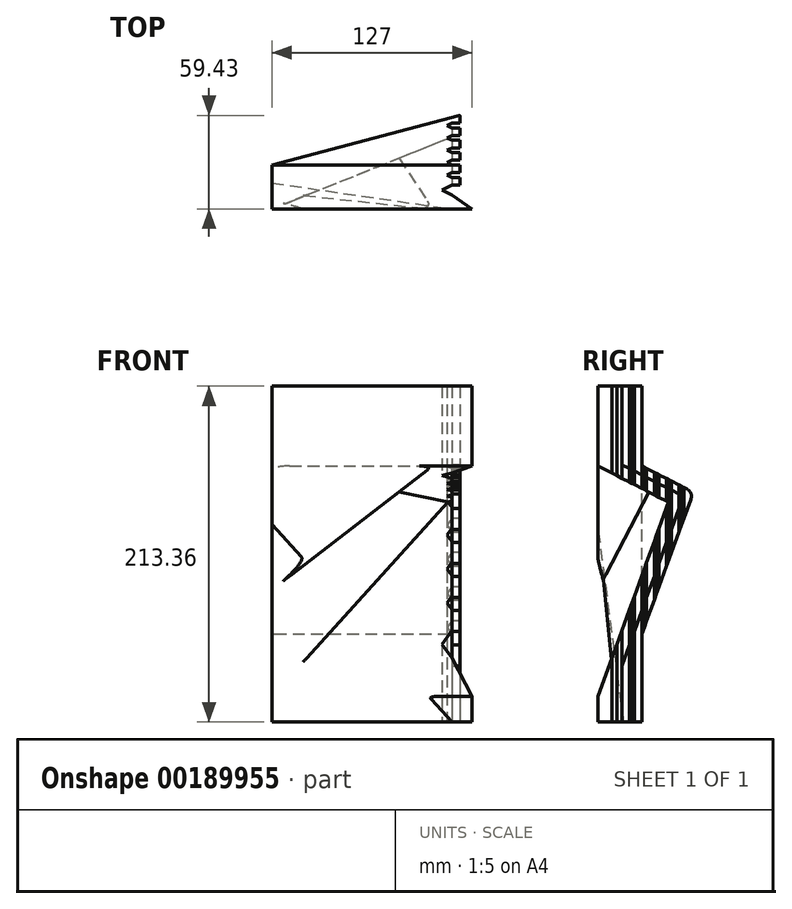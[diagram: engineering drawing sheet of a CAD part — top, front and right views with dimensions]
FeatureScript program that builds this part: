
annotation { "Feature Type Name" : "Feature", "Feature Type Description" : "" }
export const myFeature = defineFeature(function(context is Context, id is Id, definition is map)
    precondition{}
    {
        {
            var Q0;
            Q0=qCreatedBy(makeId("Top.planeOp"),FACE);
            var sketch = newSketch(context, id + "F0", { "sketchPlane" : qUnion([Q0])});
            skLineSegment(sketch, "E0", {"start": v(0, 6.35) * mm, "end": v(5.08, 6.35) * mm});
            skLineSegment(sketch, "E1", {"start": v(5.08, 6.35) * mm, "end": v(5.08, 11.18) * mm});
            skLineSegment(sketch, "E2", {"start": v(5.08, 11.18) * mm, "end": v(0, 11.18) * mm});
            skLineSegment(sketch, "E3", {"start": v(0, 11.18) * mm, "end": v(0, 14.22) * mm});
            skLineSegment(sketch, "E4", {"start": v(0, 14.22) * mm, "end": v(5.08, 14.22) * mm});
            skLineSegment(sketch, "E5", {"start": v(5.08, 14.22) * mm, "end": v(5.08, 19.05) * mm});
            skLineSegment(sketch, "E6", {"start": v(5.08, 19.05) * mm, "end": v(0, 19.05) * mm});
            skLineSegment(sketch, "E7", {"start": v(0, 19.05) * mm, "end": v(0, 22.1) * mm});
            skLineSegment(sketch, "E8", {"start": v(0, 22.1) * mm, "end": v(5.08, 22.1) * mm});
            skLineSegment(sketch, "E9", {"start": v(5.08, 22.1) * mm, "end": v(5.08, 26.92) * mm});
            skLineSegment(sketch, "E10", {"start": v(5.08, 26.92) * mm, "end": v(0, 26.92) * mm});
            skLineSegment(sketch, "E11", {"start": v(0, 26.92) * mm, "end": v(0, 29.97) * mm});
            skLineSegment(sketch, "E12", {"start": v(0, 29.97) * mm, "end": v(5.08, 29.97) * mm});
            skLineSegment(sketch, "E13", {"start": v(5.08, 29.97) * mm, "end": v(5.08, 34.8) * mm});
            skLineSegment(sketch, "E14", {"start": v(5.08, 34.8) * mm, "end": v(0, 34.8) * mm});
            skLineSegment(sketch, "E15", {"start": v(0, 34.8) * mm, "end": v(0, 37.85) * mm});
            skLineSegment(sketch, "E16", {"start": v(0, 37.85) * mm, "end": v(5.08, 37.85) * mm});
            skLineSegment(sketch, "E17", {"start": v(5.08, 37.85) * mm, "end": v(5.08, 42.67) * mm});
            skLineSegment(sketch, "E18", {"start": v(5.08, 42.67) * mm, "end": v(0, 42.67) * mm});
            skLineSegment(sketch, "E19", {"start": v(-114.3, 0) * mm, "end": v(0, 0) * mm});
            skLineSegment(sketch, "E20", {"start": v(0, 0) * mm, "end": v(0, 6.35) * mm});
            skLineSegment(sketch, "E21", {"start": v(0, 42.67) * mm, "end": v(0, 45.72) * mm});
            skLineSegment(sketch, "E22", {"start": v(-114.3, 53.6) * mm, "end": v(-114.3, 0) * mm});
            skLineSegment(sketch, "E23", {"start": v(0, 45.72) * mm, "end": v(5.08, 45.72) * mm});
            skLineSegment(sketch, "E24", {"start": v(5.08, 45.72) * mm, "end": v(5.08, 50.55) * mm});
            skLineSegment(sketch, "E25", {"start": v(5.08, 50.55) * mm, "end": v(0, 50.55) * mm});
            skLineSegment(sketch, "E26", {"start": v(0, 50.55) * mm, "end": v(0, 53.6) * mm});
            skLineSegment(sketch, "E27", {"start": v(0, 53.6) * mm, "end": v(-114.3, 53.6) * mm});
            skLineSegment(sketch, "E28", {"start": v(0, 0) * mm, "end": v(0, -8.89) * mm});
            skLineSegment(sketch, "E29", {"start": v(0, -8.89) * mm, "end": v(-114.3, -8.9) * mm});
            skLineSegment(sketch, "E30", {"start": v(-114.3, -8.9) * mm, "end": v(-114.3, 0) * mm});
            skLineSegment(sketch, "E31", {"start": v(0, -8.89) * mm, "end": v(12.7, -8.89) * mm});
            skLineSegment(sketch, "E32", {"start": v(12.7, -8.89) * mm, "end": v(0, 0) * mm});
            skLineSegment(sketch, "E33", {"start": v(0, 0) * mm, "end": v(-6.35, 3.17) * mm});
            skLineSegment(sketch, "E34", {"start": v(-6.35, 3.18) * mm, "end": v(0, 6.35) * mm});
            skLineSegment(sketch, "E35", {"start": v(0, 11.18) * mm, "end": v(-3.05, 12.7) * mm});
            skLineSegment(sketch, "E36", {"start": v(-3.05, 12.7) * mm, "end": v(0, 14.22) * mm});
            skLineSegment(sketch, "E37", {"start": v(0, 19.05) * mm, "end": v(-3.05, 20.57) * mm});
            skPoint(sketch, "E37.endSnap0", {"position": v(0, 20.57) * mm});
            skLineSegment(sketch, "E38", {"start": v(-3.05, 20.57) * mm, "end": v(0, 22.1) * mm});
            skLineSegment(sketch, "E39", {"start": v(0, 26.92) * mm, "end": v(-3.05, 28.45) * mm});
            skLineSegment(sketch, "E40", {"start": v(-3.05, 28.45) * mm, "end": v(0, 29.97) * mm});
            skLineSegment(sketch, "E41", {"start": v(0, 34.8) * mm, "end": v(-3.05, 36.32) * mm});
            skLineSegment(sketch, "E42", {"start": v(-3.05, 36.32) * mm, "end": v(0, 37.85) * mm});
            skLineSegment(sketch, "E43", {"start": v(0, 42.67) * mm, "end": v(-3.05, 44.2) * mm});
            skPoint(sketch, "E43.endSnap0", {"position": v(0, 44.2) * mm});
            skLineSegment(sketch, "E44", {"start": v(-3.05, 44.2) * mm, "end": v(0, 45.72) * mm});
            skLineSegment(sketch, "E45", {"start": v(0, 50.55) * mm, "end": v(-6.41, 53.6) * mm});
            skSolve(sketch);
        }
        {
            var Q0;
            Q0=makeQuery(id+"F0.imprint","IMPRINT",FACE,{"disambiguationData":[TD([[makeQuery(id+"F0.imprint","IMPRINT",EDGE,{"derivedFrom":sQuery(id+"F0.wireOp",EDGE,"E0")}),1.0]])]});
            var Q1;
            Q1=makeQuery(id+"F0.imprint","IMPRINT",FACE,{"disambiguationData":[TD([[makeQuery(id+"F0.imprint","IMPRINT",EDGE,{"derivedFrom":sQuery(id+"F0.wireOp",EDGE,"E19")}),-1.0]])]});
            var Q2;
            Q2=makeQuery(id+"F0.imprint","IMPRINT",FACE,{"disambiguationData":[TD([[makeQuery(id+"F0.imprint","IMPRINT",EDGE,{"derivedFrom":sQuery(id+"F0.wireOp",EDGE,"E28")}),1.0]])]});
            var Q3;
            Q3 = qSketchRegion(id + "F4", true);
            extrude(context, id + "F1", {"entities" : qUnion([Q0, Q1, Q2, Q3]), "depth" : 172.72 * mm, "hasSecondDirection" : true, "secondDirectionOppositeDirection" : true, "secondDirectionDepth" : 40.64 * mm});
        }
        {
            var Q0;
            Q0=makeQuery(id+"F1.opExtrude","SWEPT_FACE",FACE,{"disambiguationData":[OSD([sQuery(id+"F0.wireOp",EDGE,"E22")])]});
            var sketch = newSketch(context, id + "F2", { "sketchPlane" : qUnion([Q0])});
            skLineSegment(sketch, "E46", {"start": v(0, 117.47) * mm, "end": v(-36, 99.06) * mm});
            skLineSegment(sketch, "E47", {"start": v(-36, 99.06) * mm, "end": v(0, 0) * mm});
            skLineSegment(sketch, "E48", {"start": v(0, 117.47) * mm, "end": v(8.9, 122.02) * mm});
            skLineSegment(sketch, "E49", {"start": v(8.89, 122.02) * mm, "end": v(8.89, -24.46) * mm});
            skLineSegment(sketch, "E50", {"start": v(8.9, -24.46) * mm, "end": v(0, 0) * mm});
            skSolve(sketch);
        }
        {
            var Q0;
            Q0 = qSketchRegion(id + "F2", true);
            extrude(context, id + "F3", {"entities" : qUnion([Q0]), "operationType" : NewBodyOperationType.REMOVE, "endBound" : BoundingType.THROUGH_ALL, "oppositeDirection" : true, "depth" : 25.4 * mm});
        }
        {
            var Q0;
            {var subQ2=sQuery(id+"F0.wireOp",EDGE,"E1");Q0=makeQuery(id+"F3.boolean.opBoolean","SPLIT",FACE,{"disambiguationData":[TD([makeQuery(id+"F3.opExtrude","SWEPT_FACE",FACE,{"disambiguationData":[OSD([sQuery(id+"F2.wireOp",EDGE,"E46")])]})])],"derivedFrom":makeQuery(id+"F1.opExtrude","SWEPT_FACE",FACE,{"disambiguationData":[OSD([subQ2])]})});}
            var sketch = newSketch(context, id + "F4", { "sketchPlane" : qUnion([Q0])});
            skLineSegment(sketch, "E51.0", {"start": v(0, 117.47) * mm, "end": v(36, 99.06) * mm});
            skLineSegment(sketch, "E52.0", {"start": v(36, 99.06) * mm, "end": v(0, 0) * mm});
            skLineSegment(sketch, "E53", {"start": v(0, 117.47) * mm, "end": v(0, 126.03) * mm});
            skLineSegment(sketch, "E54", {"start": v(0, 126.03) * mm, "end": v(45.46, 102.78) * mm});
            skLineSegment(sketch, "E55", {"start": v(45.46, 102.78) * mm, "end": v(0, -22.3) * mm});
            skLineSegment(sketch, "E56", {"start": v(0, -22.3) * mm, "end": v(0, 0) * mm});
            skSolve(sketch);
        }
        {
            var Q0;
            Q0 = qSketchRegion(id + "F4", true);
            var Q1;
            {var subQ1=sQuery(id+"F0.wireOp",EDGE,"E3");Q1=makeQuery(id+"F3.boolean.opBoolean","SPLIT",FACE,{"disambiguationData":[TD([makeQuery(id+"F3.opExtrude","SWEPT_FACE",FACE,{"disambiguationData":[OSD([sQuery(id+"F2.wireOp",EDGE,"E46")])]})])],"derivedFrom":makeQuery(id+"F1.opExtrude","SWEPT_FACE",FACE,{"disambiguationData":[OSD([subQ1])]})});}
            var Q2;
            Q2=makeQuery(id+"F3.boolean.opBoolean","INTERSECT",VERTEX,{"derivedFrom":[makeQuery(id+"F1.opExtrude","SWEPT_FACE",FACE,{"disambiguationData":[OSD([sQuery(id+"F0.wireOp",EDGE,"E0")])]}),makeQuery(id+"F1.opExtrude","SWEPT_FACE",FACE,{"disambiguationData":[OSD([sQuery(id+"F0.wireOp",EDGE,"E34")])]}),makeQuery(id+"F3.opExtrude","SWEPT_FACE",FACE,{"disambiguationData":[OSD([sQuery(id+"F2.wireOp",EDGE,"E46"),sQuery(id+"F2.wireOp",EDGE,"E48")])]})]});
            extrude(context, id + "F5", {"entities" : qUnion([Q0]), "operationType" : NewBodyOperationType.REMOVE, "endBound" : BoundingType.UP_TO_VERTEX, "oppositeDirection" : true, "endBoundEntityFace" : qUnion([Q1]), "endBoundEntityVertex" : qUnion([Q2]), "depth" : 25.4 * mm});
        }
        {
            var Q0;
            {var subQ1=sQuery(id+"F0.wireOp",EDGE,"E5");Q0=makeQuery(id+"F3.boolean.opBoolean","SPLIT",FACE,{"disambiguationData":[TD([makeQuery(id+"F3.opExtrude","SWEPT_FACE",FACE,{"disambiguationData":[OSD([sQuery(id+"F2.wireOp",EDGE,"E46")])]})])],"derivedFrom":makeQuery(id+"F1.opExtrude","SWEPT_FACE",FACE,{"disambiguationData":[OSD([subQ1])]})});}
            var sketch = newSketch(context, id + "F6", { "sketchPlane" : qUnion([Q0])});
            skLineSegment(sketch, "E57", {"start": v(19.05, 122) * mm, "end": v(53.6, 104.33) * mm});
            skLineSegment(sketch, "E58", {"start": v(53.6, 104.33) * mm, "end": v(53.6, 172.72) * mm});
            skLineSegment(sketch, "E59", {"start": v(53.6, 172.72) * mm, "end": v(19.05, 172.72) * mm});
            skLineSegment(sketch, "E60", {"start": v(19.05, 172.72) * mm, "end": v(19.05, 122) * mm});
            skPoint(sketch, "E61", {"position": v(32.73, 115) * mm});
            skPoint(sketch, "E62", {"position": v(39.45, 132.31) * mm});
            skSolve(sketch);
        }
        {
            var Q0;
            Q0 = qSketchRegion(id + "F6", true);
            var Q1;
            {var subQ2=makeQuery(id+"F3.opExtrude","SWEPT_FACE",FACE,{"disambiguationData":[OSD([sQuery(id+"F2.wireOp",EDGE,"E46")])]});var subQ5=sQuery(id+"F0.wireOp",EDGE,"E21");var subQ6=sQuery(id+"F0.wireOp",EDGE,"E20");var subQ11=sQuery(id+"F0.wireOp",EDGE,"E15");var subQ15=sQuery(id+"F0.wireOp",EDGE,"E11");var subQ19=sQuery(id+"F0.wireOp",EDGE,"E7");var subQ23=sQuery(id+"F0.wireOp",EDGE,"E3");var subQ28=makeQuery(id+"F1.opExtrude","SWEPT_FACE",FACE,{"disambiguationData":[OSD([subQ6])]});var subQ30=makeQuery(id+"F3.opExtrude","SWEPT_FACE",FACE,{"disambiguationData":[OSD([sQuery(id+"F2.wireOp",EDGE,"E47")])]});var subQ33=makeQuery(id+"F1.opExtrude","SWEPT_FACE",FACE,{"disambiguationData":[OSD([subQ11])]});var subQ36=makeQuery(id+"F1.opExtrude","SWEPT_FACE",FACE,{"disambiguationData":[OSD([subQ15])]});var subQ39=makeQuery(id+"F1.opExtrude","SWEPT_FACE",FACE,{"disambiguationData":[OSD([subQ19])]});var subQ42=makeQuery(id+"F1.opExtrude","SWEPT_FACE",FACE,{"disambiguationData":[OSD([subQ23])]});Q1=makeQuery(id+"F5.boolean.opBoolean","MERGE",FACE,{"derivedFrom":[makeQuery(id+"F1.opExtrude","SWEPT_FACE",FACE,{"disambiguationData":[OSD([subQ5])]}),makeQuery(id+"F3.boolean.opBoolean","SPLIT",FACE,{"disambiguationData":[TD([subQ30])],"derivedFrom":subQ42}),makeQuery(id+"F3.boolean.opBoolean","SPLIT",FACE,{"disambiguationData":[TD([subQ2])],"derivedFrom":subQ42}),makeQuery(id+"F3.boolean.opBoolean","SPLIT",FACE,{"disambiguationData":[TD([subQ30])],"derivedFrom":subQ39}),makeQuery(id+"F3.boolean.opBoolean","SPLIT",FACE,{"disambiguationData":[TD([subQ2])],"derivedFrom":subQ39}),makeQuery(id+"F3.boolean.opBoolean","SPLIT",FACE,{"disambiguationData":[TD([subQ30])],"derivedFrom":subQ36}),makeQuery(id+"F3.boolean.opBoolean","SPLIT",FACE,{"disambiguationData":[TD([subQ2])],"derivedFrom":subQ36}),makeQuery(id+"F3.boolean.opBoolean","SPLIT",FACE,{"disambiguationData":[TD([subQ30])],"derivedFrom":subQ33}),makeQuery(id+"F3.boolean.opBoolean","SPLIT",FACE,{"disambiguationData":[TD([subQ2])],"derivedFrom":subQ33}),makeQuery(id+"F3.boolean.opBoolean","SPLIT",FACE,{"disambiguationData":[TD([subQ30])],"derivedFrom":subQ28}),makeQuery(id+"F3.boolean.opBoolean","SPLIT",FACE,{"disambiguationData":[TD([subQ2])],"derivedFrom":subQ28}),makeQuery(id+"F5.opExtrude","CAP_FACE",FACE,{"disambiguationData":[OSD([sQuery(id+"F4.wireOp",EDGE,"r30LgNDP-MDBT-sFvh-t1dZ-1n8YGESDknUK"),sQuery(id+"F4.wireOp",EDGE,"V1CvVt0y-FSvr-zVPq-IvBo-Jav4YfUzxSMJ"),sQuery(id+"F4.wireOp",EDGE,"HjBI8CUT-Bw1e-LJHy-u5lc-1jVyPCsQLfoZ"),sQuery(id+"F4.wireOp",EDGE,"4X511eva-4H63-5xgH-bIHv-RUgGeS7ULBsc")])],"isStart":false})]});}
            extrude(context, id + "F7", {"entities" : qUnion([Q0]), "operationType" : NewBodyOperationType.REMOVE, "endBound" : BoundingType.THROUGH_ALL, "oppositeDirection" : true, "endBoundEntityFace" : qUnion([Q1]), "depth" : 25.4 * mm});
        }
        {
            var Q0;
            {var subQ1=sQuery(id+"F0.wireOp",EDGE,"E5");Q0=makeQuery(id+"F3.boolean.opBoolean","SPLIT",FACE,{"disambiguationData":[TD([makeQuery(id+"F3.opExtrude","SWEPT_FACE",FACE,{"disambiguationData":[OSD([sQuery(id+"F2.wireOp",EDGE,"E47")])]})])],"derivedFrom":makeQuery(id+"F1.opExtrude","SWEPT_FACE",FACE,{"disambiguationData":[OSD([subQ1])]})});}
            var sketch = newSketch(context, id + "F8", { "sketchPlane" : qUnion([Q0])});
            skLineSegment(sketch, "E63", {"start": v(19.05, 15.24) * mm, "end": v(56.79, 119.08) * mm});
            skLineSegment(sketch, "E64", {"start": v(56.79, 119.08) * mm, "end": v(57.02, -40.64) * mm});
            skLineSegment(sketch, "E65", {"start": v(57.02, -40.64) * mm, "end": v(19.05, -40.64) * mm});
            skLineSegment(sketch, "E66", {"start": v(19.05, -40.64) * mm, "end": v(19.05, 15.24) * mm});
            skSolve(sketch);
        }
        {
            var Q0;
            Q0 = qSketchRegion(id + "F8", true);
            extrude(context, id + "F9", {"entities" : qUnion([Q0]), "operationType" : NewBodyOperationType.REMOVE, "endBound" : BoundingType.THROUGH_ALL, "oppositeDirection" : true, "depth" : 25.4 * mm});
        }
        {
            var Q0;
            Q0=qCreatedBy(makeId("Top.planeOp"),FACE);
            var sketch = newSketch(context, id + "F10", { "sketchPlane" : qUnion([Q0])});
            skLineSegment(sketch, "E67", {"start": v(-114.3, 36) * mm, "end": v(-2.4, 36) * mm});
            skLineSegment(sketch, "E68", {"start": v(-2.4, 36) * mm, "end": v(-114.3, -8.9) * mm});
            skLineSegment(sketch, "E69", {"start": v(-114.3, -8.9) * mm, "end": v(-114.3, 36) * mm});
            skSolve(sketch);
        }
        {
            var Q0;
            Q0=makeQuery(id+"F10.imprint","IMPRINT",FACE,{"disambiguationData":[TD([[makeQuery(id+"F10.imprint","IMPRINT",EDGE,{"derivedFrom":sQuery(id+"F10.wireOp",EDGE,"E67")}),-1.0]])]});
            var Q1;
            Q1=makeQuery(id+"F3.boolean.opBoolean","COPY",FACE,{"derivedFrom":makeQuery(id+"F3.opExtrude","SWEPT_FACE",FACE,{"disambiguationData":[OSD([sQuery(id+"F2.wireOp",EDGE,"E46"),sQuery(id+"F2.wireOp",EDGE,"E48")])]})});
            var Q2;
            Q2=makeQuery(id+"F3.boolean.opBoolean","COPY",FACE,{"derivedFrom":makeQuery(id+"F3.opExtrude","SWEPT_FACE",FACE,{"disambiguationData":[OSD([sQuery(id+"F2.wireOp",EDGE,"E47"),sQuery(id+"F2.wireOp",EDGE,"E50")])]})});
            extrude(context, id + "F11", {"entities" : qUnion([Q0]), "operationType" : NewBodyOperationType.ADD, "endBound" : BoundingType.UP_TO_SURFACE, "endBoundEntityFace" : qUnion([Q1]), "depth" : 25.4 * mm, "hasSecondDirection" : true, "secondDirectionBound" : SecondDirectionBoundingType.UP_TO_SURFACE, "secondDirectionOppositeDirection" : true, "secondDirectionBoundEntityFace" : qUnion([Q2]), "secondDirectionDepth" : 25.4 * mm});
        }
        {
            var Q0;
            Q0=makeQuery(id+"F1.opExtrude","CAP_FACE",FACE,{"disambiguationData":[OSD([sQuery(id+"F0.wireOp",EDGE,"E0"),sQuery(id+"F0.wireOp",EDGE,"E1"),sQuery(id+"F0.wireOp",EDGE,"E2"),sQuery(id+"F0.wireOp",EDGE,"E3"),sQuery(id+"F0.wireOp",EDGE,"E4"),sQuery(id+"F0.wireOp",EDGE,"E5"),sQuery(id+"F0.wireOp",EDGE,"E6"),sQuery(id+"F0.wireOp",EDGE,"E7"),sQuery(id+"F0.wireOp",EDGE,"E8"),sQuery(id+"F0.wireOp",EDGE,"E9"),sQuery(id+"F0.wireOp",EDGE,"E10"),sQuery(id+"F0.wireOp",EDGE,"E11"),sQuery(id+"F0.wireOp",EDGE,"E12"),sQuery(id+"F0.wireOp",EDGE,"E13"),sQuery(id+"F0.wireOp",EDGE,"E14"),sQuery(id+"F0.wireOp",EDGE,"E15"),sQuery(id+"F0.wireOp",EDGE,"E16"),sQuery(id+"F0.wireOp",EDGE,"E17"),sQuery(id+"F0.wireOp",EDGE,"E18"),sQuery(id+"F0.wireOp",EDGE,"E20"),sQuery(id+"F0.wireOp",EDGE,"E21"),sQuery(id+"F0.wireOp",EDGE,"E22"),sQuery(id+"F0.wireOp",EDGE,"E23"),sQuery(id+"F0.wireOp",EDGE,"E24"),sQuery(id+"F0.wireOp",EDGE,"E25"),sQuery(id+"F0.wireOp",EDGE,"E26"),sQuery(id+"F0.wireOp",EDGE,"E27"),sQuery(id+"F0.wireOp",EDGE,"E29"),sQuery(id+"F0.wireOp",EDGE,"E30"),sQuery(id+"F0.wireOp",EDGE,"E31"),sQuery(id+"F0.wireOp",EDGE,"E32")])],"isStart":false});
            var sketch = newSketch(context, id + "F12", { "sketchPlane" : qUnion([Q0])});
            skLineSegment(sketch, "E70", {"start": v(-114.3, 19.05) * mm, "end": v(5.08, 50.55) * mm});
            skLineSegment(sketch, "E71", {"start": v(5.08, 50.55) * mm, "end": v(-114.3, 50.55) * mm});
            skLineSegment(sketch, "E72", {"start": v(-114.3, 50.55) * mm, "end": v(-114.3, 19.05) * mm});
            skLineSegment(sketch, "E73", {"start": v(5.08, 50.55) * mm, "end": v(14.04, 52.91) * mm});
            skLineSegment(sketch, "E74", {"start": v(14.04, 52.91) * mm, "end": v(-114.3, 52.91) * mm});
            skLineSegment(sketch, "E75", {"start": v(-114.3, 52.91) * mm, "end": v(-114.3, 50.55) * mm});
            skSolve(sketch);
        }
        {
            var Q0;
            Q0 = qSketchRegion(id + "F12", true);
            extrude(context, id + "F13", {"entities" : qUnion([Q0]), "operationType" : NewBodyOperationType.REMOVE, "endBound" : BoundingType.THROUGH_ALL, "oppositeDirection" : true, "depth" : 25.4 * mm});
        }
        {
            var Q0;
            Q0=makeQuery(id+"F13.boolean.opBoolean","INTERSECT",EDGE,{"derivedFrom":[makeQuery(id+"F9.boolean.opBoolean","COPY",FACE,{"derivedFrom":makeQuery(id+"F9.opExtrude","SWEPT_FACE",FACE,{"disambiguationData":[OSD([sQuery(id+"F8.wireOp",EDGE,"E63")])]})}),makeQuery(id+"F13.opExtrude","SWEPT_FACE",FACE,{"disambiguationData":[OSD([sQuery(id+"F12.wireOp",EDGE,"E70"),sQuery(id+"F12.wireOp",EDGE,"E73")])]})]});
            var Q1;
            Q1=makeQuery(id+"F13.boolean.opBoolean","INTERSECT",EDGE,{"derivedFrom":[makeQuery(id+"F7.boolean.opBoolean","COPY",FACE,{"derivedFrom":makeQuery(id+"F7.opExtrude","SWEPT_FACE",FACE,{"disambiguationData":[OSD([sQuery(id+"F6.wireOp",EDGE,"E57")])]})}),makeQuery(id+"F13.opExtrude","SWEPT_FACE",FACE,{"disambiguationData":[OSD([sQuery(id+"F12.wireOp",EDGE,"E70"),sQuery(id+"F12.wireOp",EDGE,"E73")])]})]});
            fillet(context, id + "F14", {"entities" : qUnion([Q0, Q1]), "radius" : 5.08 * mm, "tangentPropagation" : true, "allowEdgeOverflow" : false});
        }
        {
            var Q0;
            {var subQ1=sQuery(id+"F0.wireOp",EDGE,"E31");var subQ3=sQuery(id+"F0.wireOp",EDGE,"E29");Q0=makeQuery(id+"F3.boolean.opBoolean","SPLIT",FACE,{"disambiguationData":[TD([makeQuery(id+"F3.opExtrude","SWEPT_FACE",FACE,{"disambiguationData":[OSD([sQuery(id+"F2.wireOp",EDGE,"E46"),sQuery(id+"F2.wireOp",EDGE,"E48")])]})])],"derivedFrom":makeQuery(id+"F1.opExtrude","SWEPT_FACE",FACE,{"disambiguationData":[OSD([subQ3,subQ1])]})});}
            var sketch = newSketch(context, id + "F15", { "sketchPlane" : qUnion([Q0])});
            skLineSegment(sketch, "E76", {"start": v(-12.26, 122.02) * mm, "end": v(-114.3, 43.28) * mm});
            skLineSegment(sketch, "E77", {"start": v(-114.3, 43.28) * mm, "end": v(-114.3, 122.02) * mm});
            skLineSegment(sketch, "E78", {"start": v(-114.3, 122.02) * mm, "end": v(-12.26, 122.02) * mm});
            skSolve(sketch);
        }
        {
            var Q0;
            Q0 = qSketchRegion(id + "F15", true);
            extrude(context, id + "F16", {"entities" : qUnion([Q0]), "operationType" : NewBodyOperationType.ADD, "endBound" : BoundingType.UP_TO_NEXT, "oppositeDirection" : true, "depth" : 25.4 * mm});
        }
        {
            var Q0;
            Q0=makeQuery(id+"F2.imprint","IMPRINT",FACE,{"disambiguationData":[TD([[makeQuery(id+"F2.imprint","IMPRINT",EDGE,{"derivedFrom":sQuery(id+"F2.wireOp",EDGE,"E46")}),-1.0]])]});
            var sketch = newSketch(context, id + "F17", { "sketchPlane" : qUnion([Q0])});
            skLineSegment(sketch, "E79", {"start": v(-7.62, -40.64) * mm, "end": v(8.89, 84.77) * mm});
            skLineSegment(sketch, "E80", {"start": v(8.89, 84.77) * mm, "end": v(8.9, -40.64) * mm});
            skLineSegment(sketch, "E81", {"start": v(8.9, -40.64) * mm, "end": v(-7.62, -40.64) * mm});
            skSolve(sketch);
        }
        {
            var Q0;
            Q0=makeQuery(id+"F1.opExtrude","CAP_FACE",FACE,{"disambiguationData":[OSD([sQuery(id+"F0.wireOp",EDGE,"E0"),sQuery(id+"F0.wireOp",EDGE,"E1"),sQuery(id+"F0.wireOp",EDGE,"E2"),sQuery(id+"F0.wireOp",EDGE,"E3"),sQuery(id+"F0.wireOp",EDGE,"E4"),sQuery(id+"F0.wireOp",EDGE,"E5"),sQuery(id+"F0.wireOp",EDGE,"E6"),sQuery(id+"F0.wireOp",EDGE,"E7"),sQuery(id+"F0.wireOp",EDGE,"E8"),sQuery(id+"F0.wireOp",EDGE,"E9"),sQuery(id+"F0.wireOp",EDGE,"E10"),sQuery(id+"F0.wireOp",EDGE,"E11"),sQuery(id+"F0.wireOp",EDGE,"E12"),sQuery(id+"F0.wireOp",EDGE,"E13"),sQuery(id+"F0.wireOp",EDGE,"E14"),sQuery(id+"F0.wireOp",EDGE,"E15"),sQuery(id+"F0.wireOp",EDGE,"E16"),sQuery(id+"F0.wireOp",EDGE,"E17"),sQuery(id+"F0.wireOp",EDGE,"E18"),sQuery(id+"F0.wireOp",EDGE,"E20"),sQuery(id+"F0.wireOp",EDGE,"E21"),sQuery(id+"F0.wireOp",EDGE,"E22"),sQuery(id+"F0.wireOp",EDGE,"E23"),sQuery(id+"F0.wireOp",EDGE,"E24"),sQuery(id+"F0.wireOp",EDGE,"E25"),sQuery(id+"F0.wireOp",EDGE,"E26"),sQuery(id+"F0.wireOp",EDGE,"E27"),sQuery(id+"F0.wireOp",EDGE,"E29"),sQuery(id+"F0.wireOp",EDGE,"E30"),sQuery(id+"F0.wireOp",EDGE,"E31"),sQuery(id+"F0.wireOp",EDGE,"E32")])],"isStart":true});
            var sketch = newSketch(context, id + "F18", { "sketchPlane" : qUnion([Q0])});
            skLineSegment(sketch, "E82", {"start": v(0, 8.9) * mm, "end": v(-114.3, -7.62) * mm});
            skSolve(sketch);
        }
        {
            var Q0;
            Q0 = qSketchRegion(id + "F17", true);
            var Q1;
            Q1=sQuery(id+"F18.wireOp",EDGE,"E82");
            sweep(context, id + "F19", {"operationType" : NewBodyOperationType.REMOVE, "profiles" : qUnion([Q0]), "path" : qUnion([Q1])});
        }
        {
            var Q0;
            Q0=makeQuery(id+"F19.boolean.opBoolean","INTERSECT",EDGE,{"derivedFrom":[makeQuery(id+"F3.boolean.opBoolean","COPY",FACE,{"derivedFrom":makeQuery(id+"F3.opExtrude","SWEPT_FACE",FACE,{"disambiguationData":[OSD([sQuery(id+"F2.wireOp",EDGE,"E47"),sQuery(id+"F2.wireOp",EDGE,"E50")])]})}),makeQuery(id+"F19.opSweep","SWEPT_FACE",FACE,{"disambiguationData":[OSD([sQuery(id+"F17.wireOp",EDGE,"E79"),sQuery(id+"F18.wireOp",EDGE,"E82")])]})]});
            fillet(context, id + "F20", {"entities" : qUnion([Q0]), "radius" : 5.08 * mm, "tangentPropagation" : true, "allowEdgeOverflow" : false});
        }
        {
            var Q0;
            Q0=makeQuery(id+"F16.opExtrude","CAP_EDGE",EDGE,{"disambiguationData":[OSD([sQuery(id+"F15.wireOp",EDGE,"E76")])],"isStart":true});
            fillet(context, id + "F21", {"entities" : qUnion([Q0]), "radius" : 5.08 * mm, "tangentPropagation" : true, "allowEdgeOverflow" : false});
        }
        {
            var Q0;
            Q0=makeQuery(id+"F19.boolean.opBoolean","INTERSECT",EDGE,{"derivedFrom":[makeQuery(id+"F11.opExtrude","SWEPT_FACE",FACE,{"disambiguationData":[OSD([sQuery(id+"F10.wireOp",EDGE,"E68")])]}),makeQuery(id+"F19.opSweep","SWEPT_FACE",FACE,{"disambiguationData":[OSD([sQuery(id+"F17.wireOp",EDGE,"E79"),sQuery(id+"F18.wireOp",EDGE,"E82")])]})]});
            fillet(context, id + "F22", {"entities" : qUnion([Q0]), "radius" : 5.08 * mm, "tangentPropagation" : true, "allowEdgeOverflow" : false});
        }
    });
